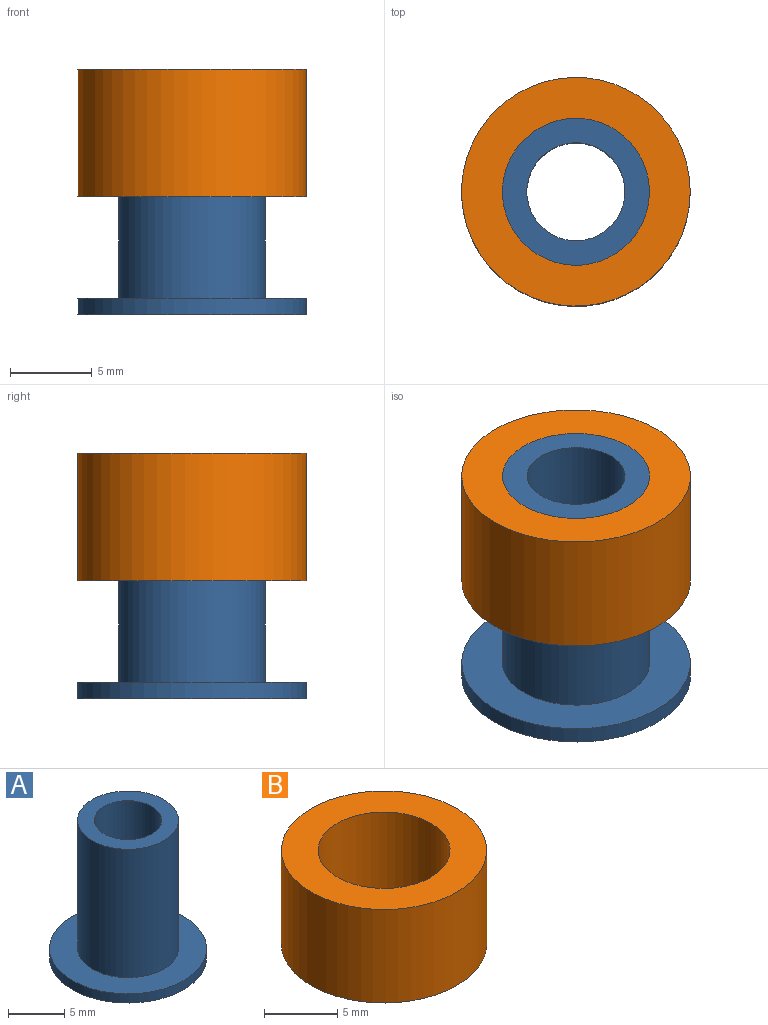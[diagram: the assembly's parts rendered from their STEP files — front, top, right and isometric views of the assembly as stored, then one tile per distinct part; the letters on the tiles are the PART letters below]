
ASSEMBLY  parts=2 mates=1
PART A: 6 faces, bbox 14x14x15 mm
  f0: cylinder r=3mm len=15mm, axis (0,0,-1), area 282.7mm2, adj f3,f5
  f1: cylinder r=7mm len=14mm, axis (0,0,-1), area 44mm2, adj f2,f3
  f2: plane 14x14mm, normal (0,0,1), area 90.3mm2, adj f1,f4
  f3: plane 14x14mm, normal (0,0,-1), area 125.7mm2, adj f0,f1
  f4: cylinder r=4.5mm len=14mm, axis (0,0,-1), area 395.8mm2, adj f2,f5
  f5: plane 9x9mm, normal (0,0,1), area 35.3mm2, adj f0,f4
PART B: 4 faces, bbox 14x14x7.8 mm
  f0: cylinder r=4.5mm len=9mm, axis (0,0,-1), area 220.5mm2, adj f2,f3
  f1: cylinder r=7mm len=14mm, axis (0,0,-1), area 343.1mm2, adj f2,f3
  f2: plane 14x14mm, normal (0,0,1), area 90.3mm2, adj f0,f1
  f3: plane 14x14mm, normal (0,0,-1), area 90.3mm2, adj f0,f1
PLACE A t=(-10,-2.91,0.39)mm
PLACE B t=(-10,-2.91,7.59)mm
MATE fastened B.f1 <-> A.f4  axis (0,0,1) through (-10,-2.91,15.39)mm
